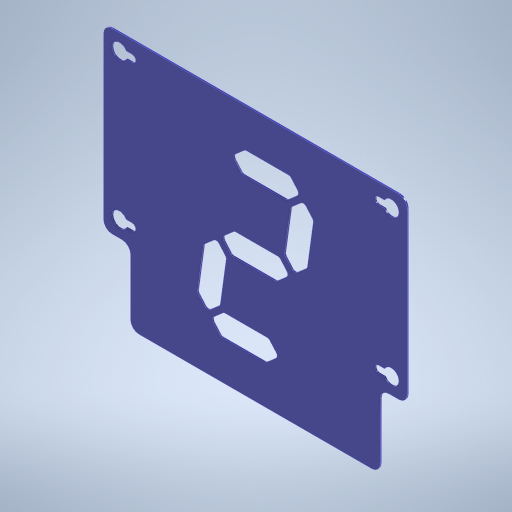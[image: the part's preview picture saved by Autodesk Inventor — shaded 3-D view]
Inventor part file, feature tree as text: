
AUTODESK INVENTOR PART (.ipt)
format: ipt  version: 2024.2 (Build 282272000, 272)  size: 486,400 bytes
history: native  units: mm
features: sketch x2, other x1, extrude x1
ambient origin geometry x8: Origin, YZ Plane, XZ Plane, XY Plane, X Axis, Y Axis, Z Axis, Center Point
bodies: Solid1 (feature_tree)
feature tree (4):
  other  "TorsoCoverFrameBasis.ipt"
  sketch  "Sketch2"  dims[d2=20.0mm d4=20.0mm d6=30.0mm d8=10.0mm d9=4.0mm d10=13.333333mm d11=13.333333mm d12=40.0mm d13=40.0mm d14=2.0mm d16=45.300052mm d17=45.300052mm d18=45.300052mm d20=10.0mm d21=1.396263mm d22=0.75mm d23=0.0mm d24=5.0mm d25=95.5mm d29=0.0mm d27=0.5mm d28=0.872665mm d30=0.872665mm d31=0.5mm d32=0.872665mm d33=0.5mm d34=0.872665mm]
  extrude  "Extrusion1"  Depth=5.0mm
  sketch  "Sketch1"  dims[d0=10.0mm]
